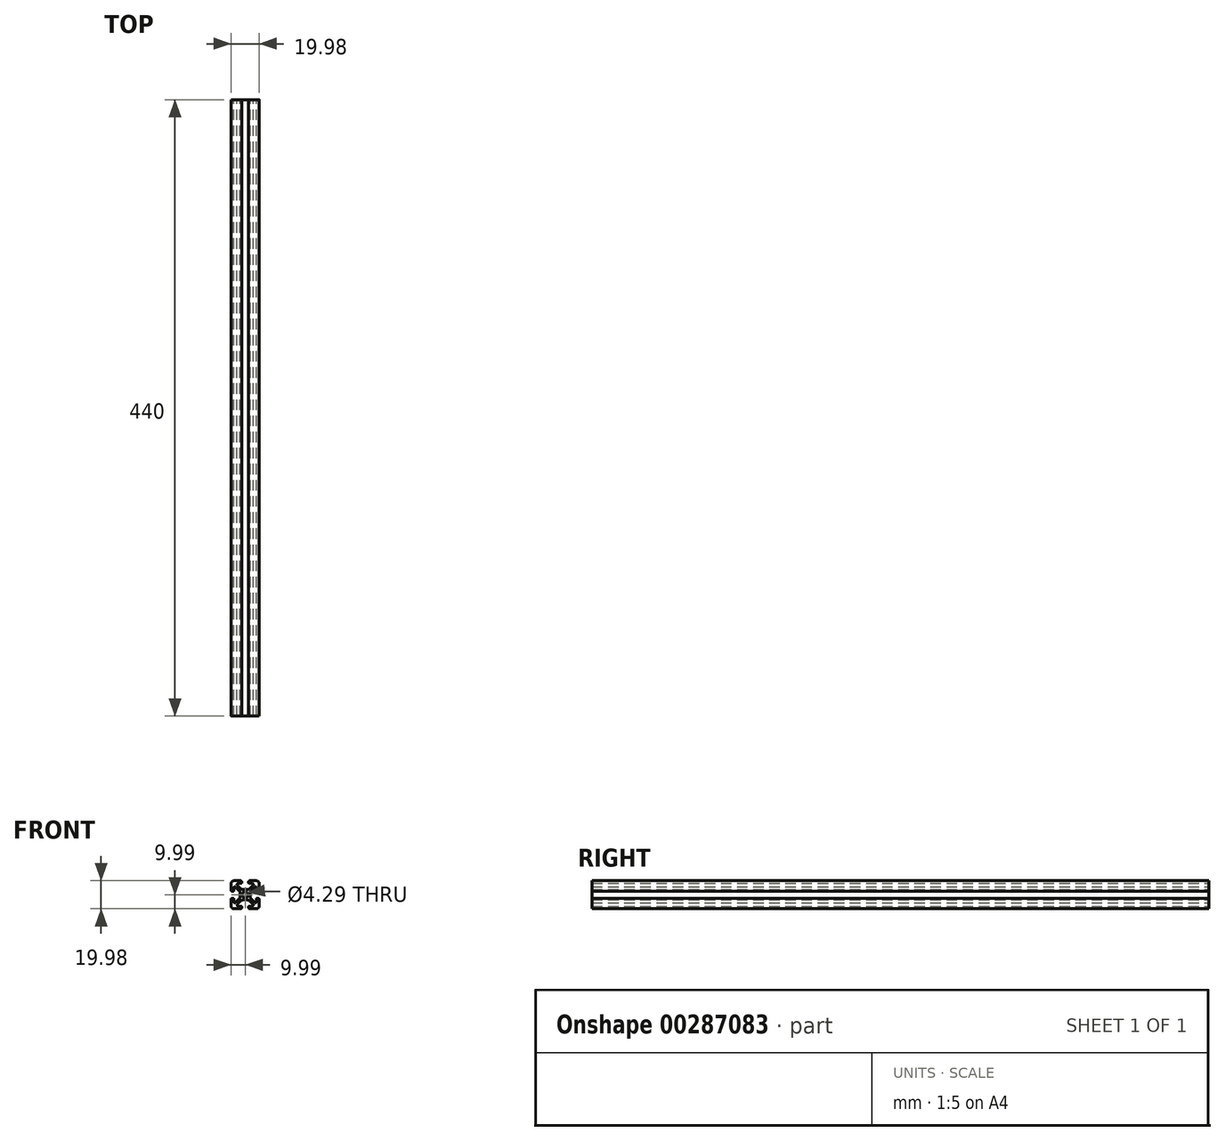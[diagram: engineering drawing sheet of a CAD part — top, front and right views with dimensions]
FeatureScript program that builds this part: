
annotation { "Feature Type Name" : "Feature", "Feature Type Description" : "" }
export const myFeature = defineFeature(function(context is Context, id is Id, definition is map)
    precondition{}
    {
        {
            var Q0;
            Q0=qCreatedBy(makeId("Front.planeOp"),FACE);
            var sketch = newSketch(context, id + "F0", { "sketchPlane" : qUnion([Q0])});
            skLineSegment(sketch, "E0", {"start": v(-7.99, 10) * mm, "end": v(-3.29, 10) * mm});
            skArc(sketch, "E1", {"start": v(-3.29, 10) * mm, "mid": v(-2.73, 9.76) * mm, "end": v(-2.5, 9.2) * mm});
            skLineSegment(sketch, "E2", {"start": v(-2.5, 9.2) * mm, "end": v(-2.5, 8.5) * mm});
            skLineSegment(sketch, "E3", {"start": v(-5.5, 6.76) * mm, "end": v(-3.25, 4.5) * mm});
            skArc(sketch, "E4", {"start": v(-4.91, 8.2) * mm, "mid": v(-5.69, 7.67) * mm, "end": v(-5.5, 6.76) * mm});
            skLineSegment(sketch, "E5", {"start": v(3.29, 10) * mm, "end": v(7.99, 10) * mm});
            skArc(sketch, "E6", {"start": v(2.5, 9.2) * mm, "mid": v(2.73, 9.76) * mm, "end": v(3.29, 10) * mm});
            skLineSegment(sketch, "E7", {"start": v(3.25, 4.5) * mm, "end": v(5.5, 6.76) * mm});
            skArc(sketch, "E8", {"start": v(1.13, 3.63) * mm, "mid": v(2.28, 3.86) * mm, "end": v(3.25, 4.5) * mm});
            skArc(sketch, "E9", {"start": v(7.99, 10) * mm, "mid": v(9.4, 9.4) * mm, "end": v(10, 7.99) * mm});
            skLineSegment(sketch, "E10", {"start": v(-2.8, 8.2) * mm, "end": v(-4.91, 8.2) * mm});
            skArc(sketch, "E11", {"start": v(-2.5, 8.5) * mm, "mid": v(-2.6, 8.28) * mm, "end": v(-2.8, 8.2) * mm});
            skLineSegment(sketch, "E12", {"start": v(4.91, 8.2) * mm, "end": v(2.8, 8.2) * mm});
            skLineSegment(sketch, "E13", {"start": v(2.5, 8.5) * mm, "end": v(2.5, 9.2) * mm});
            skArc(sketch, "E14", {"start": v(2.8, 8.2) * mm, "mid": v(2.6, 8.28) * mm, "end": v(2.5, 8.5) * mm});
            skArc(sketch, "E15", {"start": v(5.5, 6.76) * mm, "mid": v(5.69, 7.67) * mm, "end": v(4.91, 8.2) * mm});
            skLineSegment(sketch, "E16", {"start": v(-1.13, 3.63) * mm, "end": v(1.13, 3.63) * mm});
            skArc(sketch, "E17", {"start": v(-3.25, 4.5) * mm, "mid": v(-2.28, 3.86) * mm, "end": v(-1.13, 3.63) * mm});
            skArc(sketch, "E18", {"start": v(-10, 7.99) * mm, "mid": v(-9.4, 9.4) * mm, "end": v(-7.99, 10) * mm});
            skLineSegment(sketch, "E19", {"start": v(10, 7.99) * mm, "end": v(10, 3.29) * mm});
            skLineSegment(sketch, "E20", {"start": v(4.5, -3.25) * mm, "end": v(6.76, -5.5) * mm});
            skArc(sketch, "E21", {"start": v(3.63, -1.13) * mm, "mid": v(3.86, -2.28) * mm, "end": v(4.5, -3.25) * mm});
            skLineSegment(sketch, "E22", {"start": v(3.63, 1.13) * mm, "end": v(3.63, -1.13) * mm});
            skArc(sketch, "E23", {"start": v(9.2, -2.5) * mm, "mid": v(9.76, -2.73) * mm, "end": v(10, -3.29) * mm});
            skLineSegment(sketch, "E24", {"start": v(10, -3.29) * mm, "end": v(10, -7.99) * mm});
            skLineSegment(sketch, "E25", {"start": v(8.5, -2.5) * mm, "end": v(9.2, -2.5) * mm});
            skLineSegment(sketch, "E26", {"start": v(-9.2, -2.5) * mm, "end": v(-8.5, -2.5) * mm});
            skArc(sketch, "E27", {"start": v(-10, -3.29) * mm, "mid": v(-9.76, -2.73) * mm, "end": v(-9.2, -2.5) * mm});
            skLineSegment(sketch, "E28", {"start": v(-8.2, -2.8) * mm, "end": v(-8.2, -4.91) * mm});
            skLineSegment(sketch, "E29", {"start": v(-10, 3.29) * mm, "end": v(-10, 7.99) * mm});
            skArc(sketch, "E30", {"start": v(-9.2, 2.5) * mm, "mid": v(-9.76, 2.73) * mm, "end": v(-10, 3.29) * mm});
            skLineSegment(sketch, "E31", {"start": v(-4.5, 3.25) * mm, "end": v(-6.76, 5.5) * mm});
            skLineSegment(sketch, "E32", {"start": v(-3.63, -1.13) * mm, "end": v(-3.63, 1.13) * mm});
            skArc(sketch, "E33", {"start": v(-3.63, 1.13) * mm, "mid": v(-3.86, 2.28) * mm, "end": v(-4.5, 3.25) * mm});
            skArc(sketch, "E34", {"start": v(-6.76, 5.5) * mm, "mid": v(-7.67, 5.69) * mm, "end": v(-8.2, 4.91) * mm});
            skLineSegment(sketch, "E35", {"start": v(-8.5, 2.5) * mm, "end": v(-9.2, 2.5) * mm});
            skLineSegment(sketch, "E36", {"start": v(8.2, 2.8) * mm, "end": v(8.2, 4.91) * mm});
            skArc(sketch, "E37", {"start": v(8.2, 4.91) * mm, "mid": v(7.67, 5.69) * mm, "end": v(6.76, 5.5) * mm});
            skLineSegment(sketch, "E38", {"start": v(-10, -7.99) * mm, "end": v(-10, -3.29) * mm});
            skArc(sketch, "E39", {"start": v(-4.5, -3.25) * mm, "mid": v(-3.86, -2.28) * mm, "end": v(-3.63, -1.13) * mm});
            skLineSegment(sketch, "E40", {"start": v(-6.76, -5.5) * mm, "end": v(-4.5, -3.25) * mm});
            skLineSegment(sketch, "E41", {"start": v(1.13, -3.63) * mm, "end": v(-1.13, -3.63) * mm});
            skLineSegment(sketch, "E42", {"start": v(5.5, -6.76) * mm, "end": v(3.25, -4.5) * mm});
            skArc(sketch, "E43", {"start": v(3.25, -4.5) * mm, "mid": v(2.28, -3.86) * mm, "end": v(1.13, -3.63) * mm});
            skLineSegment(sketch, "E44", {"start": v(8.2, -4.91) * mm, "end": v(8.2, -2.8) * mm});
            skLineSegment(sketch, "E45", {"start": v(-4.91, -8.2) * mm, "end": v(-2.8, -8.2) * mm});
            skArc(sketch, "E46", {"start": v(-5.5, -6.76) * mm, "mid": v(-5.69, -7.67) * mm, "end": v(-4.91, -8.2) * mm});
            skArc(sketch, "E47", {"start": v(-8.2, -4.91) * mm, "mid": v(-7.67, -5.69) * mm, "end": v(-6.76, -5.5) * mm});
            skArc(sketch, "E48", {"start": v(-8.5, -2.5) * mm, "mid": v(-8.28, -2.6) * mm, "end": v(-8.2, -2.8) * mm});
            skArc(sketch, "E49", {"start": v(4.91, -8.2) * mm, "mid": v(5.69, -7.67) * mm, "end": v(5.5, -6.76) * mm});
            skLineSegment(sketch, "E50", {"start": v(2.5, -9.2) * mm, "end": v(2.5, -8.5) * mm});
            skArc(sketch, "E51", {"start": v(2.5, -8.5) * mm, "mid": v(2.6, -8.28) * mm, "end": v(2.8, -8.2) * mm});
            skLineSegment(sketch, "E52", {"start": v(2.8, -8.2) * mm, "end": v(4.91, -8.2) * mm});
            skArc(sketch, "E53", {"start": v(3.29, -10) * mm, "mid": v(2.73, -9.76) * mm, "end": v(2.5, -9.2) * mm});
            skArc(sketch, "E54", {"start": v(6.76, -5.5) * mm, "mid": v(7.67, -5.69) * mm, "end": v(8.2, -4.91) * mm});
            skArc(sketch, "E55", {"start": v(10, -7.99) * mm, "mid": v(9.4, -9.4) * mm, "end": v(7.99, -10) * mm});
            skArc(sketch, "E56", {"start": v(4.5, 3.25) * mm, "mid": v(3.86, 2.28) * mm, "end": v(3.63, 1.13) * mm});
            skLineSegment(sketch, "E57", {"start": v(-3.25, -4.5) * mm, "end": v(-5.5, -6.76) * mm});
            skLineSegment(sketch, "E58", {"start": v(-2.5, -8.5) * mm, "end": v(-2.5, -9.2) * mm});
            skArc(sketch, "E59", {"start": v(-2.8, -8.2) * mm, "mid": v(-2.6, -8.28) * mm, "end": v(-2.5, -8.5) * mm});
            skArc(sketch, "E60", {"start": v(-2.5, -9.2) * mm, "mid": v(-2.73, -9.76) * mm, "end": v(-3.29, -10) * mm});
            skArc(sketch, "E61", {"start": v(-1.13, -3.63) * mm, "mid": v(-2.28, -3.86) * mm, "end": v(-3.25, -4.5) * mm});
            skArc(sketch, "E62", {"start": v(10, 3.29) * mm, "mid": v(9.76, 2.73) * mm, "end": v(9.2, 2.5) * mm});
            skLineSegment(sketch, "E63", {"start": v(6.76, 5.5) * mm, "end": v(4.5, 3.25) * mm});
            skLineSegment(sketch, "E64", {"start": v(-8.2, 4.91) * mm, "end": v(-8.2, 2.8) * mm});
            skLineSegment(sketch, "E65", {"start": v(-3.29, -10) * mm, "end": v(-7.99, -10) * mm});
            skArc(sketch, "E66", {"start": v(-7.99, -10) * mm, "mid": v(-9.4, -9.4) * mm, "end": v(-10, -7.99) * mm});
            skLineSegment(sketch, "E67", {"start": v(7.99, -10) * mm, "end": v(3.29, -10) * mm});
            skLineSegment(sketch, "E68", {"start": v(9.2, 2.5) * mm, "end": v(8.5, 2.5) * mm});
            skArc(sketch, "E69", {"start": v(8.5, 2.5) * mm, "mid": v(8.28, 2.6) * mm, "end": v(8.2, 2.8) * mm});
            skCircle(sketch, "E70", {"center": v(0, 0) * mm, "radius": 2.15 * mm});
            skArc(sketch, "E71", {"start": v(-8.2, 2.8) * mm, "mid": v(-8.28, 2.6) * mm, "end": v(-8.5, 2.5) * mm});
            skArc(sketch, "E72", {"start": v(8.2, -2.8) * mm, "mid": v(8.28, -2.6) * mm, "end": v(8.5, -2.5) * mm});
            skSolve(sketch);
        }
        {
            var Q0;
            Q0=qSketchRegion(id+"F0",true);
            extrude(context, id + "F1", {"entities" : qUnion([Q0]), "depth" : 440 * mm});
        }
    });
